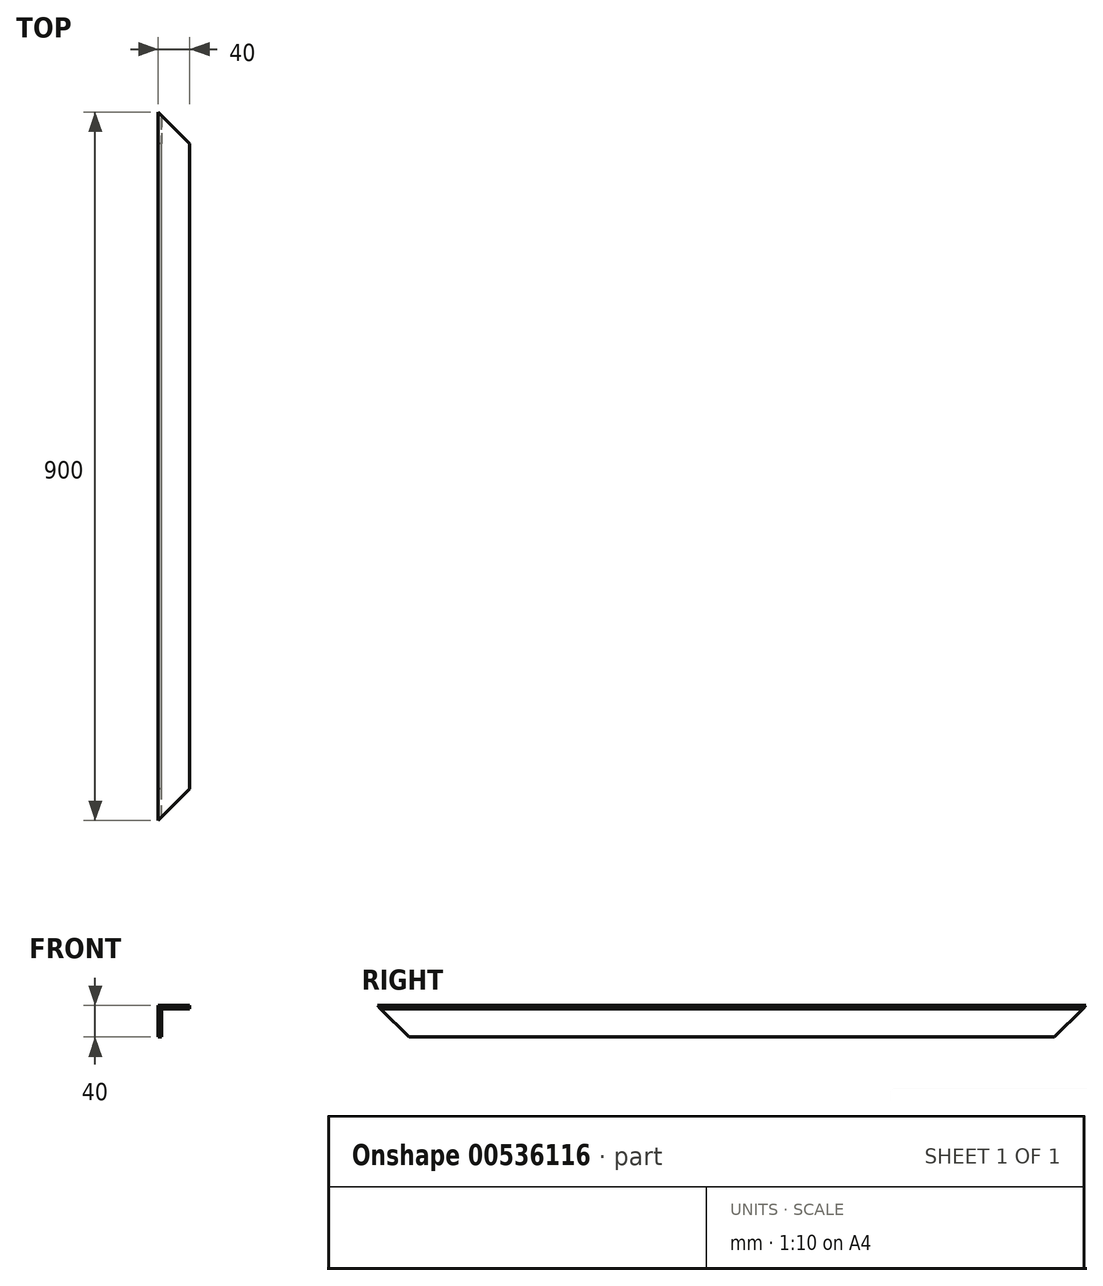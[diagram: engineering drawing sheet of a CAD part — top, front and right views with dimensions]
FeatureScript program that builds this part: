
annotation { "Feature Type Name" : "Feature", "Feature Type Description" : "" }
export const myFeature = defineFeature(function(context is Context, id is Id, definition is map)
    precondition{}
    {
        {
            var Q0;
            Q0=qCreatedBy(makeId("Front.planeOp"),FACE);
            var sketch = newSketch(context, id + "F0", { "sketchPlane" : qUnion([Q0])});
            skLineSegment(sketch, "E0", {"start": v(0, 0) * mm, "end": v(0, 40) * mm});
            skLineSegment(sketch, "E1", {"start": v(0, 40) * mm, "end": v(40, 40) * mm});
            skLineSegment(sketch, "E2.0", {"start": v(4, 36) * mm, "end": v(40, 36) * mm});
            skLineSegment(sketch, "E2.1", {"start": v(4, 0) * mm, "end": v(4, 36) * mm});
            skLineSegment(sketch, "E3", {"start": v(0, 0) * mm, "end": v(4, 0) * mm});
            skLineSegment(sketch, "E4", {"start": v(40, 36) * mm, "end": v(40, 40) * mm});
            skSolve(sketch);
        }
        {
            var Q0;
            Q0=makeQuery(id+"F0.imprint","IMPRINT",FACE,{"disambiguationData":[TD([[makeQuery(id+"F0.imprint","IMPRINT",EDGE,{"derivedFrom":sQuery(id+"F0.wireOp",EDGE,"E0")}),-1.0]])]});
            extrude(context, id + "F1", {"entities" : qUnion([Q0]), "endBound" : BoundingType.SYMMETRIC, "depth" : 900 * mm, "offsetDistance" : 25 * mm});
        }
        {
            var Q0;
            Q0=makeQuery(id+"F1.opExtrude","SWEPT_FACE",FACE,{"disambiguationData":[OSD([sQuery(id+"F0.wireOp",EDGE,"E0")])]});
            var sketch = newSketch(context, id + "F2", { "sketchPlane" : qUnion([Q0])});
            skLineSegment(sketch, "E5", {"start": v(-450, 40) * mm, "end": v(-410, 0) * mm});
            skLineSegment(sketch, "E6", {"start": v(450, 40) * mm, "end": v(410, 0) * mm});
            skSolve(sketch);
        }
        {
            var Q0;
            {var subQ0=sQuery(id+"F2.wireOp",EDGE,"E5");Q0=makeQuery(id+"F2.imprint","IMPRINT",FACE,{"disambiguationData":[TD([[makeQuery(id+"F2.imprint","IMPRINT",EDGE,{"derivedFrom":subQ0}),-1.0]])]});}
            var Q1;
            {var subQ0=sQuery(id+"F2.wireOp",EDGE,"E6");Q1=makeQuery(id+"F2.imprint","IMPRINT",FACE,{"disambiguationData":[TD([[makeQuery(id+"F2.imprint","IMPRINT",EDGE,{"derivedFrom":subQ0}),1.0]])]});}
            extrude(context, id + "F3", {"entities" : qUnion([Q0, Q1]), "operationType" : NewBodyOperationType.REMOVE, "oppositeDirection" : true, "depth" : 40 * mm, "offsetDistance" : 25 * mm});
        }
        {
            var Q0;
            Q0=makeQuery(id+"F1.opExtrude","SWEPT_FACE",FACE,{"disambiguationData":[OSD([sQuery(id+"F0.wireOp",EDGE,"E1")])]});
            var sketch = newSketch(context, id + "F4", { "sketchPlane" : qUnion([Q0])});
            skLineSegment(sketch, "E7", {"start": v(0, 450) * mm, "end": v(40, 410) * mm});
            skLineSegment(sketch, "E8", {"start": v(0, -450) * mm, "end": v(40, -410) * mm});
            skSolve(sketch);
        }
        {
            var Q0;
            {var subQ0=sQuery(id+"F4.wireOp",EDGE,"E7");Q0=makeQuery(id+"F4.imprint","IMPRINT",FACE,{"disambiguationData":[TD([[makeQuery(id+"F4.imprint","IMPRINT",EDGE,{"derivedFrom":subQ0}),1.0]])]});}
            var Q1;
            {var subQ0=sQuery(id+"F4.wireOp",EDGE,"E8");Q1=makeQuery(id+"F4.imprint","IMPRINT",FACE,{"disambiguationData":[TD([[makeQuery(id+"F4.imprint","IMPRINT",EDGE,{"derivedFrom":subQ0}),-1.0]])]});}
            extrude(context, id + "F5", {"entities" : qUnion([Q0, Q1]), "operationType" : NewBodyOperationType.REMOVE, "oppositeDirection" : true, "depth" : 40 * mm, "offsetDistance" : 25 * mm});
        }
    });
